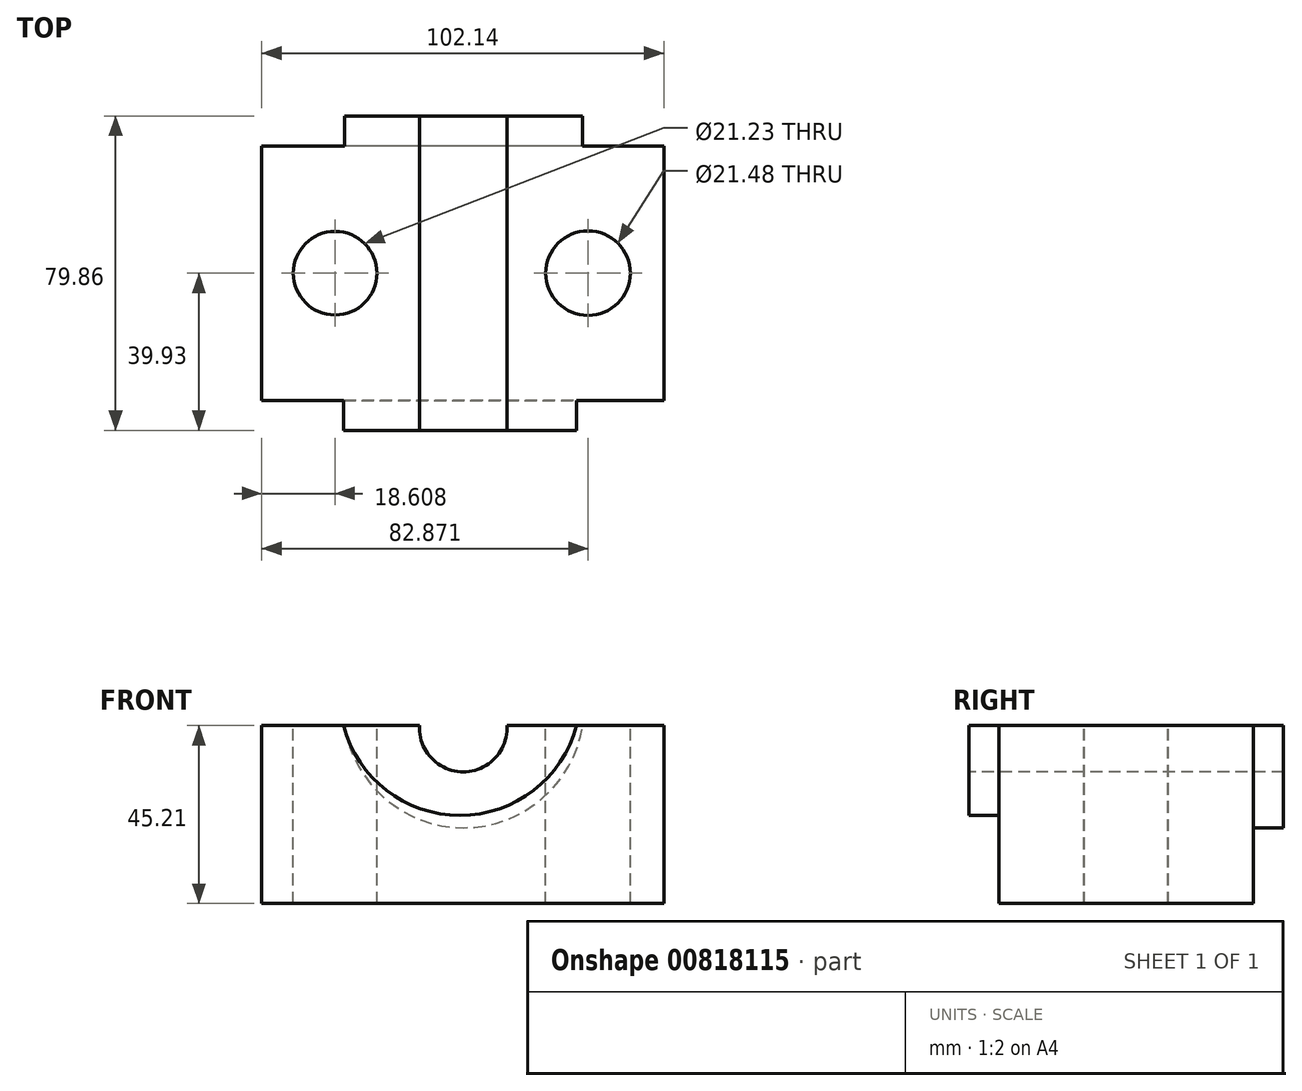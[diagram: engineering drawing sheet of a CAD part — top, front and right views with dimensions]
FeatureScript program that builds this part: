
annotation { "Feature Type Name" : "Feature", "Feature Type Description" : "" }
export const myFeature = defineFeature(function(context is Context, id is Id, definition is map)
    precondition{}
    {
        {
            var Q0;
            Q0=qCreatedBy(makeId("Top.planeOp"),FACE);
            var sketch = newSketch(context, id + "F0", { "sketchPlane" : qUnion([Q0])});
            skLineSegment(sketch, "E0.bottom", {"start": v(51.07, 39.93) * mm, "end": v(-51.07, 39.93) * mm});
            skLineSegment(sketch, "E0.top", {"start": v(51.07, -39.93) * mm, "end": v(-51.07, -39.93) * mm});
            skLineSegment(sketch, "E0.left", {"start": v(51.07, 39.93) * mm, "end": v(51.07, -39.93) * mm});
            skLineSegment(sketch, "E0.right", {"start": v(-51.07, 39.93) * mm, "end": v(-51.07, -39.93) * mm});
            skPoint(sketch, "E0.middle", {"position": v(0, 0) * mm});
            skSolve(sketch);
        }
        {
            var Q0;
            Q0=qSketchRegion(id+"F0",true);
            var Q1;
            Q1=makeQuery(id+"F0.imprint","IMPRINT",FACE,{"disambiguationData":[TD([[makeQuery(id+"F0.imprint","IMPRINT",EDGE,{"derivedFrom":sQuery(id+"F0.wireOp",EDGE,"E0.bottom")}),1.0]])]});
            extrude(context, id + "F1", {"entities" : qUnion([Q0, Q1]), "depth" : 45.2 * mm, "offsetDistance" : 25.4 * mm});
        }
        {
            var Q0;
            Q0=makeQuery(id+"F1.opExtrude","SWEPT_FACE",FACE,{"disambiguationData":[OSD([sQuery(id+"F0.wireOp",EDGE,"E0.bottom")])]});
            var sketch = newSketch(context, id + "F2", { "sketchPlane" : qUnion([Q0])});
            skArc(sketch, "E1", {"start": v(-30.42, 45.21) * mm, "mid": v(-0.18, 19.25) * mm, "end": v(30.07, 45.21) * mm});
            skSolve(sketch);
        }
        {
            var Q0;
            {var subQ3=sQuery(id+"F2.wireOp",EDGE,"E1");Q0=makeQuery(id+"F2.imprint","IMPRINT",FACE,{"disambiguationData":[TD([[makeQuery(id+"F2.imprint","IMPRINT",EDGE,{"derivedFrom":subQ3}),-1.0]])]});}
            extrude(context, id + "F3", {"entities" : qUnion([Q0]), "operationType" : NewBodyOperationType.REMOVE, "oppositeDirection" : true, "depth" : 7.62 * mm, "offsetDistance" : 25.4 * mm});
        }
        {
            var Q0;
            Q0=makeQuery(id+"F1.opExtrude","SWEPT_FACE",FACE,{"disambiguationData":[OSD([sQuery(id+"F0.wireOp",EDGE,"E0.top")])]});
            var sketch = newSketch(context, id + "F4", { "sketchPlane" : qUnion([Q0])});
            skArc(sketch, "E2", {"start": v(-30.32, 45.21) * mm, "mid": v(-0.72, 22.38) * mm, "end": v(28.88, 45.21) * mm});
            skSolve(sketch);
        }
        {
            var Q0;
            {var subQ3=sQuery(id+"F4.wireOp",EDGE,"E2");Q0=makeQuery(id+"F4.imprint","IMPRINT",FACE,{"disambiguationData":[TD([[makeQuery(id+"F4.imprint","IMPRINT",EDGE,{"derivedFrom":subQ3}),-1.0]])]});}
            extrude(context, id + "F5", {"entities" : qUnion([Q0]), "operationType" : NewBodyOperationType.REMOVE, "oppositeDirection" : true, "depth" : 7.62 * mm, "offsetDistance" : 25.4 * mm});
        }
        {
            var Q0;
            Q0=makeQuery(id+"F1.opExtrude","CAP_FACE",FACE,{"disambiguationData":[OSD([sQuery(id+"F0.wireOp",EDGE,"E0.bottom"),sQuery(id+"F0.wireOp",EDGE,"E0.top"),sQuery(id+"F0.wireOp",EDGE,"E0.left"),sQuery(id+"F0.wireOp",EDGE,"E0.right")])],"isStart":false});
            var sketch = newSketch(context, id + "F6", { "sketchPlane" : qUnion([Q0])});
            skLineSegment(sketch, "E3.bottom", {"start": v(10.98, 39.93) * mm, "end": v(-10.98, 39.93) * mm});
            skLineSegment(sketch, "E3.top", {"start": v(10.98, -39.93) * mm, "end": v(-10.98, -39.93) * mm});
            skLineSegment(sketch, "E3.left", {"start": v(10.98, 39.93) * mm, "end": v(10.98, -39.93) * mm});
            skLineSegment(sketch, "E3.right", {"start": v(-10.98, 39.93) * mm, "end": v(-10.98, -39.93) * mm});
            skPoint(sketch, "E3.middle", {"position": v(0, 0) * mm});
            skSolve(sketch);
        }
        {
            var Q0;
            Q0=makeQuery(id+"F1.opExtrude","SWEPT_FACE",FACE,{"disambiguationData":[OSD([sQuery(id+"F0.wireOp",EDGE,"E0.top")])]});
            var sketch = newSketch(context, id + "F7", { "sketchPlane" : qUnion([Q0])});
            skArc(sketch, "E4", {"start": v(-11, 45.21) * mm, "mid": v(0.1, 33.45) * mm, "end": v(11.2, 45.21) * mm});
            skSolve(sketch);
        }
        {
            var Q0;
            {var subQ0=sQuery(id+"F7.wireOp",EDGE,"E4");Q0=makeQuery(id+"F7.imprint","IMPRINT",FACE,{"disambiguationData":[TD([[makeQuery(id+"F7.imprint","IMPRINT",EDGE,{"derivedFrom":subQ0}),1.0]])]});}
            extrude(context, id + "F8", {"entities" : qUnion([Q0]), "operationType" : NewBodyOperationType.REMOVE, "oppositeDirection" : true, "depth" : 240.8 * mm, "offsetDistance" : 25.4 * mm});
        }
        {
            var Q0;
            {var subQ12=sQuery(id+"F6.wireOp",EDGE,"E3.right");Q0=makeQuery(id+"F6.imprint","IMPRINT",FACE,{"disambiguationData":[TD([[makeQuery(id+"F6.imprint","IMPRINT",EDGE,{"derivedFrom":subQ12}),-1.0]])]});}
            var sketch = newSketch(context, id + "F9", { "sketchPlane" : qUnion([Q0])});
            skCircle(sketch, "E5", {"center": v(-32.46, 0) * mm, "radius": 10.61 * mm});
            skCircle(sketch, "E6", {"center": v(31.8, 0) * mm, "radius": 10.74 * mm});
            skSolve(sketch);
        }
        {
            var Q0;
            Q0=qSketchRegion(id+"F9",true);
            extrude(context, id + "F10", {"entities" : qUnion([Q0]), "operationType" : NewBodyOperationType.REMOVE, "oppositeDirection" : true, "depth" : 83.57 * mm, "offsetDistance" : 25.4 * mm});
        }
    });
